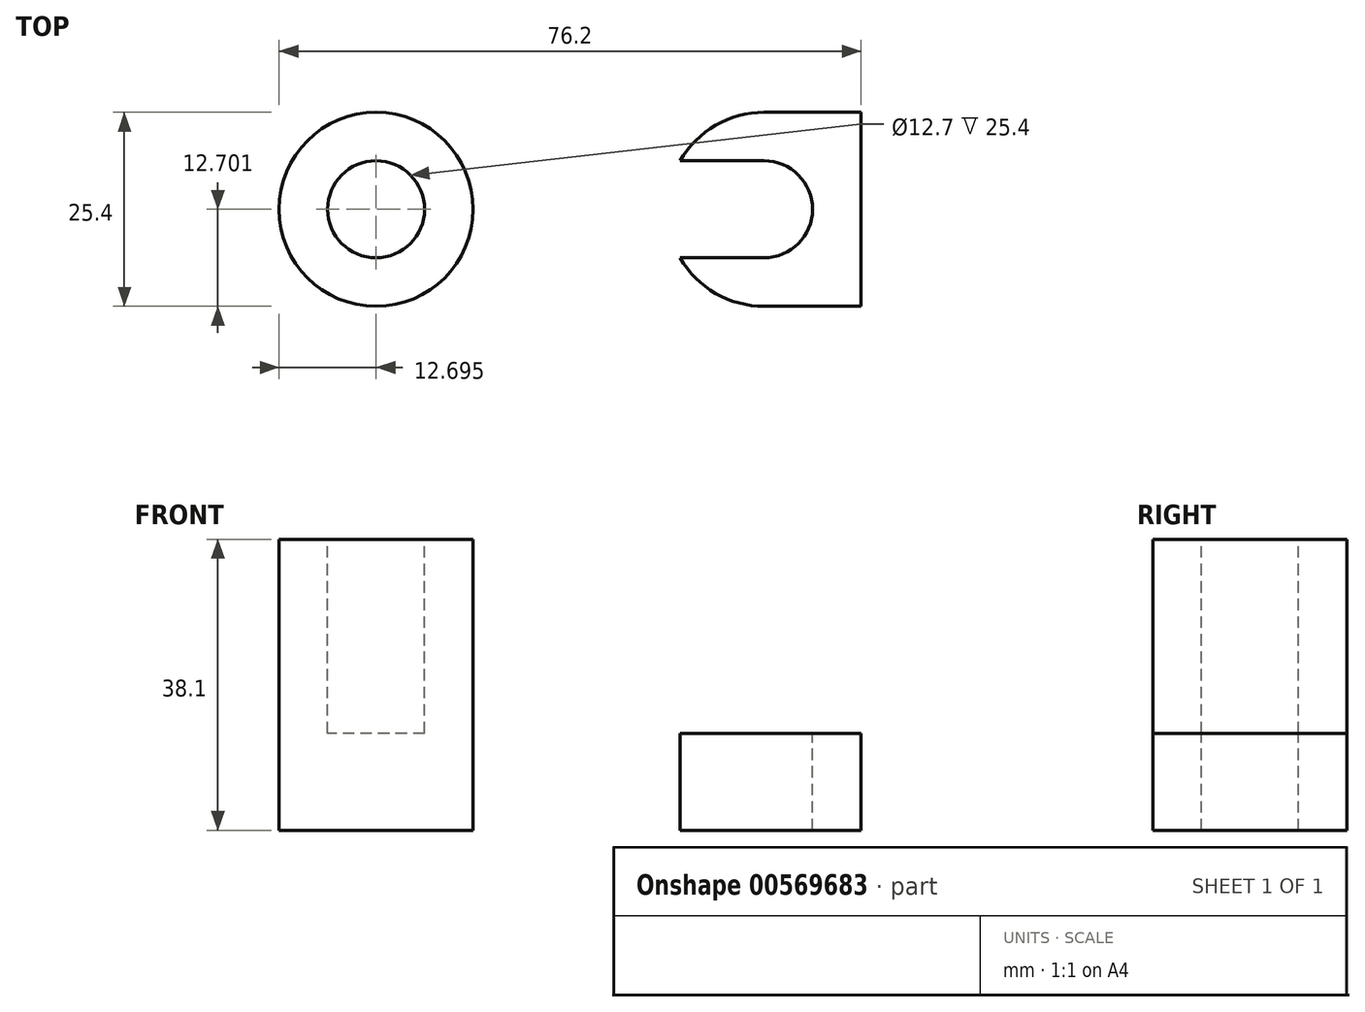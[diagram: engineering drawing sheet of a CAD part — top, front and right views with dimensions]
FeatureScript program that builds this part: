
annotation { "Feature Type Name" : "Feature", "Feature Type Description" : "" }
export const myFeature = defineFeature(function(context is Context, id is Id, definition is map)
    precondition{}
    {
        {
            var Q0;
            Q0=qCreatedBy(makeId("Top.planeOp"),FACE);
            var sketch = newSketch(context, id + "F0", { "sketchPlane" : qUnion([Q0])});
            skLineSegment(sketch, "E0.bottom", {"start": v(-7.86, -8.67) * mm, "end": v(68.34, -8.67) * mm});
            skLineSegment(sketch, "E0.top", {"start": v(-7.86, 16.73) * mm, "end": v(68.34, 16.73) * mm});
            skLineSegment(sketch, "E0.left", {"start": v(-7.86, -8.67) * mm, "end": v(-7.86, 16.73) * mm});
            skLineSegment(sketch, "E0.right", {"start": v(68.34, -8.67) * mm, "end": v(68.34, 16.73) * mm});
            skSolve(sketch);
        }
        {
            var Q0;
            Q0 = qSketchRegion(id + "F0", true);
            extrude(context, id + "F1", {"entities" : qUnion([Q0]), "depth" : 38.1 * mm, "offsetDistance" : 25.4 * mm});
        }
        {
            var Q0;
            Q0=makeQuery(id+"F1.opExtrude","SWEPT_FACE",FACE,{"disambiguationData":[OSD([sQuery(id+"F0.wireOp",EDGE,"E0.bottom")])]});
            var sketch = newSketch(context, id + "F2", { "sketchPlane" : qUnion([Q0])});
            skLineSegment(sketch, "E1", {"start": v(17.54, 38.1) * mm, "end": v(17.54, 12.7) * mm});
            skLineSegment(sketch, "E2", {"start": v(17.54, 12.7) * mm, "end": v(68.34, 12.7) * mm});
            skLineSegment(sketch, "E3", {"start": v(68.34, 12.7) * mm, "end": v(68.34, 38.1) * mm});
            skLineSegment(sketch, "E4", {"start": v(68.34, 38.1) * mm, "end": v(17.54, 38.1) * mm});
            skSolve(sketch);
        }
        {
            var Q0;
            Q0 = qSketchRegion(id + "F2", true);
            extrude(context, id + "F3", {"entities" : qUnion([Q0]), "operationType" : NewBodyOperationType.REMOVE, "oppositeDirection" : true, "depth" : 25.4 * mm, "offsetDistance" : 25.4 * mm});
        }
        {
            var Q0;
            Q0=makeQuery(id+"F1.opExtrude","CAP_FACE",FACE,{"disambiguationData":[OSD([sQuery(id+"F0.wireOp",EDGE,"E0.bottom"),sQuery(id+"F0.wireOp",EDGE,"E0.top"),sQuery(id+"F0.wireOp",EDGE,"E0.left"),sQuery(id+"F0.wireOp",EDGE,"E0.right")])],"isStart":false});
            var sketch = newSketch(context, id + "F4", { "sketchPlane" : qUnion([Q0])});
            skLineSegment(sketch, "E5", {"start": v(-1.51, 4.03) * mm, "end": v(11.19, 4.03) * mm});
            skCircle(sketch, "E6", {"center": v(4.84, 4.03) * mm, "radius": 6.35 * mm});
            skPoint(sketch, "E7.orphan", {"position": v(-7.86, 4.03) * mm});
            skPoint(sketch, "E8.orphan", {"position": v(17.54, 4.03) * mm});
            skSolve(sketch);
        }
        {
            var Q0;
            Q0 = qSketchRegion(id + "F4", true);
            extrude(context, id + "F5", {"entities" : qUnion([Q0]), "operationType" : NewBodyOperationType.REMOVE, "oppositeDirection" : true, "depth" : 25.4 * mm, "offsetDistance" : 25.4 * mm});
        }
        {
            var Q0;
            Q0=makeQuery(id+"F1.opExtrude","CAP_FACE",FACE,{"disambiguationData":[OSD([sQuery(id+"F0.wireOp",EDGE,"E0.bottom"),sQuery(id+"F0.wireOp",EDGE,"E0.top"),sQuery(id+"F0.wireOp",EDGE,"E0.left"),sQuery(id+"F0.wireOp",EDGE,"E0.right")])],"isStart":false});
            var sketch = newSketch(context, id + "F6", { "sketchPlane" : qUnion([Q0])});
            skCircle(sketch, "E9", {"center": v(4.84, 4.03) * mm, "radius": 12.7 * mm});
            skSolve(sketch);
        }
        {
            var Q0;
            {var subQ0=sQuery(id+"F6.wireOp",EDGE,"E9");var subQ1=makeQuery(id+"F1.opExtrude","CAP_EDGE",EDGE,{"disambiguationData":[OSD([sQuery(id+"F0.wireOp",EDGE,"E0.top")])],"isStart":false});var subQ2=makeQuery(id+"F6.imprint","INTERSECT",VERTEX,{"derivedFrom":[subQ1,subQ0]});Q0=makeQuery(id+"F6.imprint","IMPRINT",FACE,{"disambiguationData":[TD([[makeQuery(id+"F6.imprint","IMPRINT",EDGE,{"disambiguationData":[TD([[subQ2,-1.0]])],"derivedFrom":subQ0}),-1.0]])]});}
            var Q1;
            {var subQ0=sQuery(id+"F6.wireOp",EDGE,"E9");var subQ1=makeQuery(id+"F1.opExtrude","CAP_EDGE",EDGE,{"disambiguationData":[OSD([sQuery(id+"F0.wireOp",EDGE,"E0.left")])],"isStart":false});var subQ2=makeQuery(id+"F6.imprint","INTERSECT",VERTEX,{"derivedFrom":[subQ1,subQ0]});Q1=makeQuery(id+"F6.imprint","IMPRINT",FACE,{"disambiguationData":[TD([[makeQuery(id+"F6.imprint","IMPRINT",EDGE,{"disambiguationData":[TD([[subQ2,-1.0]])],"derivedFrom":subQ0}),-1.0]])]});}
            var Q2;
            {var subQ0=sQuery(id+"F6.wireOp",EDGE,"E9");var subQ1=sQuery(id+"F0.wireOp",EDGE,"E0.bottom");var subQ4=makeQuery(id+"F1.opExtrude","CAP_EDGE",EDGE,{"disambiguationData":[OSD([subQ1])],"isStart":false});var subQ5=makeQuery(id+"F6.imprint","INTERSECT",VERTEX,{"derivedFrom":[subQ4,subQ0]});Q2=makeQuery(id+"F6.imprint","IMPRINT",FACE,{"disambiguationData":[TD([[makeQuery(id+"F6.imprint","IMPRINT",EDGE,{"disambiguationData":[TD([[subQ5,-1.0]])],"derivedFrom":subQ0}),-1.0]])]});}
            var Q3;
            {var subQ0=sQuery(id+"F6.wireOp",EDGE,"E9");var subQ1=makeQuery(id+"F1.opExtrude","CAP_EDGE",EDGE,{"disambiguationData":[OSD([sQuery(id+"F0.wireOp",EDGE,"E0.top")])],"isStart":false});var subQ2=makeQuery(id+"F6.imprint","INTERSECT",VERTEX,{"derivedFrom":[subQ1,subQ0]});Q3=makeQuery(id+"F6.imprint","IMPRINT",FACE,{"disambiguationData":[TD([[makeQuery(id+"F6.imprint","IMPRINT",EDGE,{"disambiguationData":[TD([[subQ2,1.0]])],"derivedFrom":subQ0}),-1.0]])]});}
            extrude(context, id + "F7", {"entities" : qUnion([Q0, Q1, Q2, Q3]), "operationType" : NewBodyOperationType.REMOVE, "oppositeDirection" : true, "depth" : 25.4 * mm, "offsetDistance" : 25.4 * mm});
        }
        {
            var Q0;
            Q0=makeQuery(id+"F7.boolean.opBoolean","COPY",FACE,{"derivedFrom":makeQuery(id+"F7.opExtrude","CAP_FACE",FACE,{"disambiguationData":[OSD([sQuery(id+"F0.wireOp",EDGE,"E0.top"),sQuery(id+"F0.wireOp",EDGE,"E0.left"),sQuery(id+"F6.wireOp",EDGE,"E9")])],"isStart":false})});
            var Q1;
            Q1=makeQuery(id+"F7.boolean.opBoolean","COPY",FACE,{"derivedFrom":makeQuery(id+"F7.opExtrude","CAP_FACE",FACE,{"disambiguationData":[OSD([sQuery(id+"F0.wireOp",EDGE,"E0.bottom"),sQuery(id+"F0.wireOp",EDGE,"E0.left"),sQuery(id+"F6.wireOp",EDGE,"E9")])],"isStart":false})});
            extrude(context, id + "F8", {"entities" : qUnion([Q0, Q1]), "operationType" : NewBodyOperationType.REMOVE, "oppositeDirection" : true, "depth" : 25.4 * mm, "offsetDistance" : 25.4 * mm});
        }
        {
            var Q0;
            {var subQ0=sQuery(id+"F6.wireOp",EDGE,"E9");var subQ1=sQuery(id+"F2.wireOp",EDGE,"E4");var subQ2=sQuery(id+"F2.wireOp",EDGE,"E1");var subQ3=sQuery(id+"F0.wireOp",EDGE,"E0.bottom");Q0=makeQuery(id+"F7.boolean.opBoolean","MERGE",FACE,{"derivedFrom":[makeQuery(id+"F3.boolean.opBoolean","COPY",FACE,{"derivedFrom":makeQuery(id+"F3.opExtrude","SWEPT_FACE",FACE,{"disambiguationData":[OSD([sQuery(id+"F2.wireOp",EDGE,"E2")])]})}),makeQuery(id+"F7.opExtrude","CAP_FACE",FACE,{"disambiguationData":[OSD([subQ3,sQuery(id+"F0.wireOp",EDGE,"E0.top"),subQ2,subQ1,subQ0])],"isStart":false}),makeQuery(id+"F7.opExtrude","CAP_FACE",FACE,{"disambiguationData":[OSD([subQ3,subQ2,subQ1,subQ0])],"isStart":false})]});}
            var sketch = newSketch(context, id + "F9", { "sketchPlane" : qUnion([Q0])});
            skLineSegment(sketch, "E10", {"start": v(68.34, 16.73) * mm, "end": v(55.64, 16.73) * mm});
            skArc(sketch, "E11", {"start": v(55.64, -2.32) * mm, "mid": v(61.99, 4.03) * mm, "end": v(55.64, 10.38) * mm});
            skLineSegment(sketch, "E12", {"start": v(17.54, 16.73) * mm, "end": v(30.24, 16.73) * mm});
            skPoint(sketch, "E12.startSnap0", {"position": v(17.54, 4.03) * mm});
            skArc(sketch, "E13", {"start": v(30.24, 10.38) * mm, "mid": v(23.89, 4.03) * mm, "end": v(30.24, -2.32) * mm});
            skPoint(sketch, "E14.orphan", {"position": v(55.64, -8.67) * mm});
            skPoint(sketch, "E15.orphan", {"position": v(30.24, -8.67) * mm});
            skLineSegment(sketch, "E16", {"start": v(55.64, 10.38) * mm, "end": v(30.24, 10.38) * mm});
            skLineSegment(sketch, "E17", {"start": v(55.64, -2.32) * mm, "end": v(30.24, -2.32) * mm});
            skSolve(sketch);
        }
        {
            var Q0;
            Q0 = qSketchRegion(id + "F9", true);
            extrude(context, id + "F10", {"entities" : qUnion([Q0]), "operationType" : NewBodyOperationType.REMOVE, "oppositeDirection" : true, "depth" : 25.4 * mm, "offsetDistance" : 25.4 * mm});
        }
        {
            var Q0;
            {var subQ0=sQuery(id+"F6.wireOp",EDGE,"E9");var subQ1=sQuery(id+"F2.wireOp",EDGE,"E4");var subQ2=sQuery(id+"F2.wireOp",EDGE,"E1");var subQ3=sQuery(id+"F0.wireOp",EDGE,"E0.bottom");Q0=makeQuery(id+"F7.boolean.opBoolean","MERGE",FACE,{"derivedFrom":[makeQuery(id+"F3.boolean.opBoolean","COPY",FACE,{"derivedFrom":makeQuery(id+"F3.opExtrude","SWEPT_FACE",FACE,{"disambiguationData":[OSD([sQuery(id+"F2.wireOp",EDGE,"E2")])]})}),makeQuery(id+"F7.opExtrude","CAP_FACE",FACE,{"disambiguationData":[OSD([subQ3,sQuery(id+"F0.wireOp",EDGE,"E0.top"),subQ2,subQ1,subQ0])],"isStart":false}),makeQuery(id+"F7.opExtrude","CAP_FACE",FACE,{"disambiguationData":[OSD([subQ3,subQ2,subQ1,subQ0])],"isStart":false})]});}
            var sketch = newSketch(context, id + "F11", { "sketchPlane" : qUnion([Q0])});
            skCircle(sketch, "E18", {"center": v(55.64, 4.03) * mm, "radius": 12.7 * mm});
            skSolve(sketch);
        }
        {
            var Q0;
            {var subQ0=sQuery(id+"F11.wireOp",EDGE,"E18");var subQ1=sQuery(id+"F0.wireOp",EDGE,"E0.top");var subQ2=makeQuery(id+"F1.opExtrude","CAP_EDGE",EDGE,{"disambiguationData":[OSD([subQ1])],"isStart":false});var subQ4=sQuery(id+"F2.wireOp",EDGE,"E2");var subQ5=makeQuery(id+"F7.boolean.opBoolean","MERGE",EDGE,{"derivedFrom":[makeQuery(id+"F3.boolean.opBoolean","COPY",EDGE,{"derivedFrom":makeQuery(id+"F3.opExtrude","CAP_EDGE",EDGE,{"disambiguationData":[OSD([subQ4])],"isStart":false})}),makeQuery(id+"F7.opExtrude","CAP_EDGE",EDGE,{"disambiguationData":[OSD([subQ1]),TDD([makeQuery(id+"F6.imprint","IMPRINT",EDGE,{"disambiguationData":[TD([[makeQuery(id+"F6.imprint","INTERSECT",VERTEX,{"derivedFrom":[subQ2,sQuery(id+"F6.wireOp",EDGE,"E9")]}),-1.0]])],"derivedFrom":subQ2})])],"isStart":false})]});var subQ6=makeQuery(id+"F11.imprint","INTERSECT",VERTEX,{"derivedFrom":[subQ5,subQ0]});Q0=makeQuery(id+"F11.imprint","IMPRINT",FACE,{"disambiguationData":[TD([[makeQuery(id+"F11.imprint","IMPRINT",EDGE,{"disambiguationData":[TD([[subQ6,1.0]])],"derivedFrom":subQ0}),-1.0]])]});}
            var Q1;
            {var subQ0=sQuery(id+"F11.wireOp",EDGE,"E18");var subQ1=sQuery(id+"F2.wireOp",EDGE,"E2");var subQ2=sQuery(id+"F0.wireOp",EDGE,"E0.bottom");var subQ5=makeQuery(id+"F1.opExtrude","CAP_EDGE",EDGE,{"disambiguationData":[OSD([subQ2])],"isStart":false});var subQ6=makeQuery(id+"F7.boolean.opBoolean","MERGE",EDGE,{"derivedFrom":[makeQuery(id+"F3.boolean.opBoolean","COPY",EDGE,{"derivedFrom":makeQuery(id+"F3.opExtrude","CAP_EDGE",EDGE,{"disambiguationData":[OSD([subQ1])],"isStart":true})}),makeQuery(id+"F7.opExtrude","CAP_EDGE",EDGE,{"disambiguationData":[OSD([subQ2]),TDD([makeQuery(id+"F6.imprint","IMPRINT",EDGE,{"disambiguationData":[TD([[makeQuery(id+"F6.imprint","INTERSECT",VERTEX,{"derivedFrom":[subQ5,sQuery(id+"F6.wireOp",EDGE,"E9")]}),-1.0]])],"derivedFrom":subQ5})])],"isStart":false})]});var subQ7=makeQuery(id+"F11.imprint","INTERSECT",VERTEX,{"derivedFrom":[subQ6,subQ0]});Q1=makeQuery(id+"F11.imprint","IMPRINT",FACE,{"disambiguationData":[TD([[makeQuery(id+"F11.imprint","IMPRINT",EDGE,{"disambiguationData":[TD([[subQ7,-1.0]])],"derivedFrom":subQ0}),-1.0]])]});}
            extrude(context, id + "F12", {"entities" : qUnion([Q0, Q1]), "operationType" : NewBodyOperationType.REMOVE, "oppositeDirection" : true, "depth" : 25.4 * mm, "offsetDistance" : 25.4 * mm});
        }
    });
